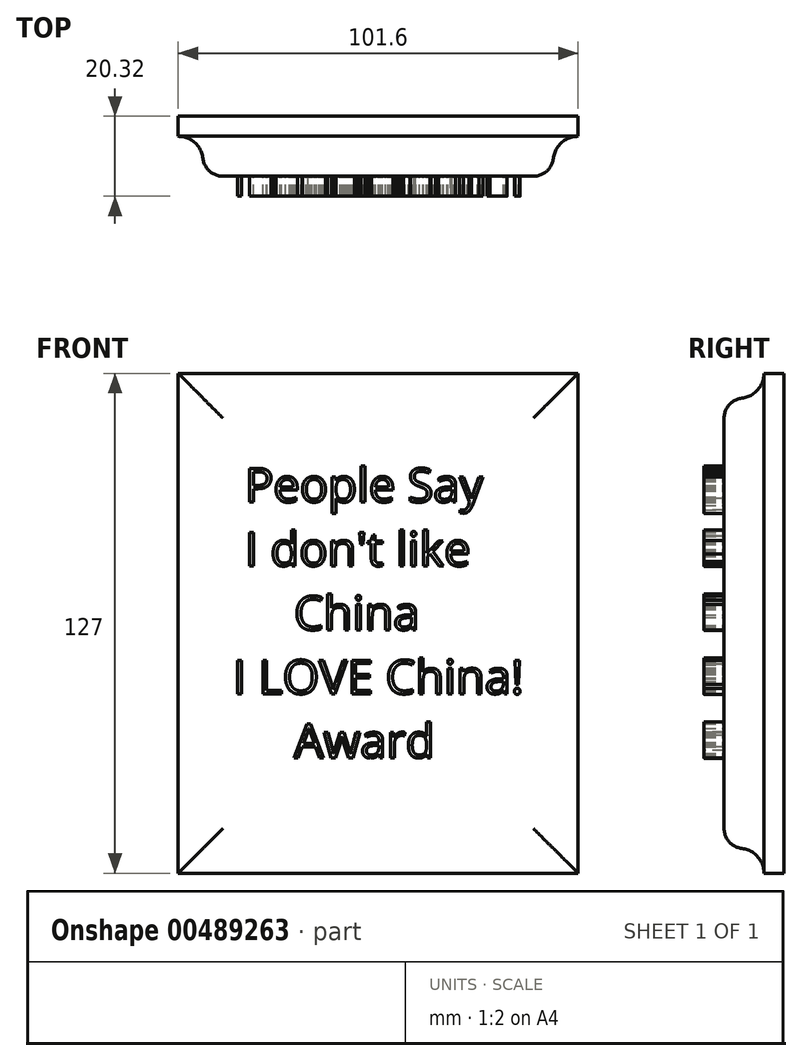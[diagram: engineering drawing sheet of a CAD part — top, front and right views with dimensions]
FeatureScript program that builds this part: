
annotation { "Feature Type Name" : "Feature", "Feature Type Description" : "" }
export const myFeature = defineFeature(function(context is Context, id is Id, definition is map)
    precondition{}
    {
        {
            var Q0;
            Q0=qCreatedBy(makeId("Front.planeOp"),FACE);
            var sketch = newSketch(context, id + "F0", { "sketchPlane" : qUnion([Q0])});
            skLineSegment(sketch, "E0.bottom", {"start": v(-101.6, 127) * mm, "end": v(0, 127) * mm});
            skLineSegment(sketch, "E0.top", {"start": v(-101.6, 0) * mm, "end": v(0, 0) * mm});
            skLineSegment(sketch, "E0.left", {"start": v(-101.6, 127) * mm, "end": v(-101.6, 0) * mm});
            skLineSegment(sketch, "E0.right", {"start": v(0, 127) * mm, "end": v(0, 0) * mm});
            skSolve(sketch);
        }
        {
            var Q0;
            Q0=qSketchRegion(id+"F0",true);
            extrude(context, id + "F1", {"entities" : qUnion([Q0]), "depth" : 15.24 * mm});
        }
        {
            var Q0;
            Q0=makeQuery(id+"F1.opExtrude","CAP_FACE",FACE,{"disambiguationData":[OSD([sQuery(id+"F0.wireOp",EDGE,"E0.bottom"),sQuery(id+"F0.wireOp",EDGE,"E0.top"),sQuery(id+"F0.wireOp",EDGE,"E0.left"),sQuery(id+"F0.wireOp",EDGE,"E0.right")])],"isStart":false});
            var sketch = newSketch(context, id + "F2", { "sketchPlane" : qUnion([Q0])});
            skLineSegment(sketch, "E1.bottom", {"start": v(-6.35, 6.35) * mm, "end": v(-95.25, 6.35) * mm});
            skLineSegment(sketch, "E1.top", {"start": v(-6.35, 120.65) * mm, "end": v(-95.25, 120.65) * mm});
            skLineSegment(sketch, "E1.left", {"start": v(-6.35, 6.35) * mm, "end": v(-6.35, 120.65) * mm});
            skLineSegment(sketch, "E1.right", {"start": v(-95.25, 6.35) * mm, "end": v(-95.25, 120.65) * mm});
            skLineSegment(sketch, "E2.bottom", {"start": v(-101.6, 127) * mm, "end": v(0, 127) * mm});
            skLineSegment(sketch, "E2.top", {"start": v(-101.6, 0) * mm, "end": v(0, 0) * mm});
            skLineSegment(sketch, "E2.left", {"start": v(-101.6, 127) * mm, "end": v(-101.6, 0) * mm});
            skLineSegment(sketch, "E2.right", {"start": v(0, 127) * mm, "end": v(0, 0) * mm});
            skSolve(sketch);
        }
        {
            var Q0;
            Q0=qSketchRegion(id+"F2",true);
            extrude(context, id + "F3", {"entities" : qUnion([Q0]), "operationType" : NewBodyOperationType.REMOVE, "oppositeDirection" : true, "depth" : 10.16 * mm});
        }
        {
            var Q0;
            Q0=makeQuery(id+"F3.boolean.opBoolean","COPY",EDGE,{"derivedFrom":makeQuery(id+"F3.opExtrude","CAP_EDGE",EDGE,{"disambiguationData":[OSD([sQuery(id+"F2.wireOp",EDGE,"E1.top")])],"isStart":false})});
            var Q1;
            Q1=makeQuery(id+"F3.boolean.opBoolean","COPY",EDGE,{"derivedFrom":makeQuery(id+"F3.opExtrude","CAP_EDGE",EDGE,{"disambiguationData":[OSD([sQuery(id+"F2.wireOp",EDGE,"E1.left")])],"isStart":false})});
            var Q2;
            Q2=makeQuery(id+"F3.boolean.opBoolean","COPY",EDGE,{"derivedFrom":makeQuery(id+"F3.opExtrude","CAP_EDGE",EDGE,{"disambiguationData":[OSD([sQuery(id+"F2.wireOp",EDGE,"E1.right")])],"isStart":false})});
            var Q3;
            Q3=makeQuery(id+"F3.boolean.opBoolean","COPY",EDGE,{"derivedFrom":makeQuery(id+"F3.opExtrude","CAP_EDGE",EDGE,{"disambiguationData":[OSD([sQuery(id+"F2.wireOp",EDGE,"E1.bottom")])],"isStart":false})});
            fillet(context, id + "F4", {"entities" : qUnion([Q0, Q1, Q2, Q3]), "radius" : 6.35 * mm, "tangentPropagation" : true, "allowEdgeOverflow" : false});
        }
        {
            var Q0;
            Q0=makeQuery(id+"F1.opExtrude","CAP_FACE",FACE,{"disambiguationData":[OSD([sQuery(id+"F0.wireOp",EDGE,"E0.bottom"),sQuery(id+"F0.wireOp",EDGE,"E0.top"),sQuery(id+"F0.wireOp",EDGE,"E0.left"),sQuery(id+"F0.wireOp",EDGE,"E0.right")])],"isStart":false});
            fillet(context, id + "F5", {"entities" : qUnion([Q0]), "radius" : 5.08 * mm, "tangentPropagation" : true, "allowEdgeOverflow" : false});
        }
        {
            var Q0;
            Q0=makeQuery(id+"F1.opExtrude","CAP_FACE",FACE,{"disambiguationData":[OSD([sQuery(id+"F0.wireOp",EDGE,"E0.bottom"),sQuery(id+"F0.wireOp",EDGE,"E0.top"),sQuery(id+"F0.wireOp",EDGE,"E0.left"),sQuery(id+"F0.wireOp",EDGE,"E0.right")])],"isStart":false});
            var sketch = newSketch(context, id + "F6", { "sketchPlane" : qUnion([Q0])});
            skText(sketch, "E3", { "text": " People Say\n I don\'t like\n     China\nI LOVE China!\n     Award", "fontName": "OpenSans-Regular.ttf"});
            const initialGuessF6  = {"E3": [-0.0877, 0.09433, 1, 0, 0.0086]};
            skSetInitialGuess(sketch, initialGuessF6);
            skSolve(sketch);
        }
        {
            var Q0;
            Q0=qSketchRegion(id+"F6",true);
            extrude(context, id + "F7", {"entities" : qUnion([Q0]), "operationType" : NewBodyOperationType.ADD, "depth" : 5.08 * mm});
        }
    });
